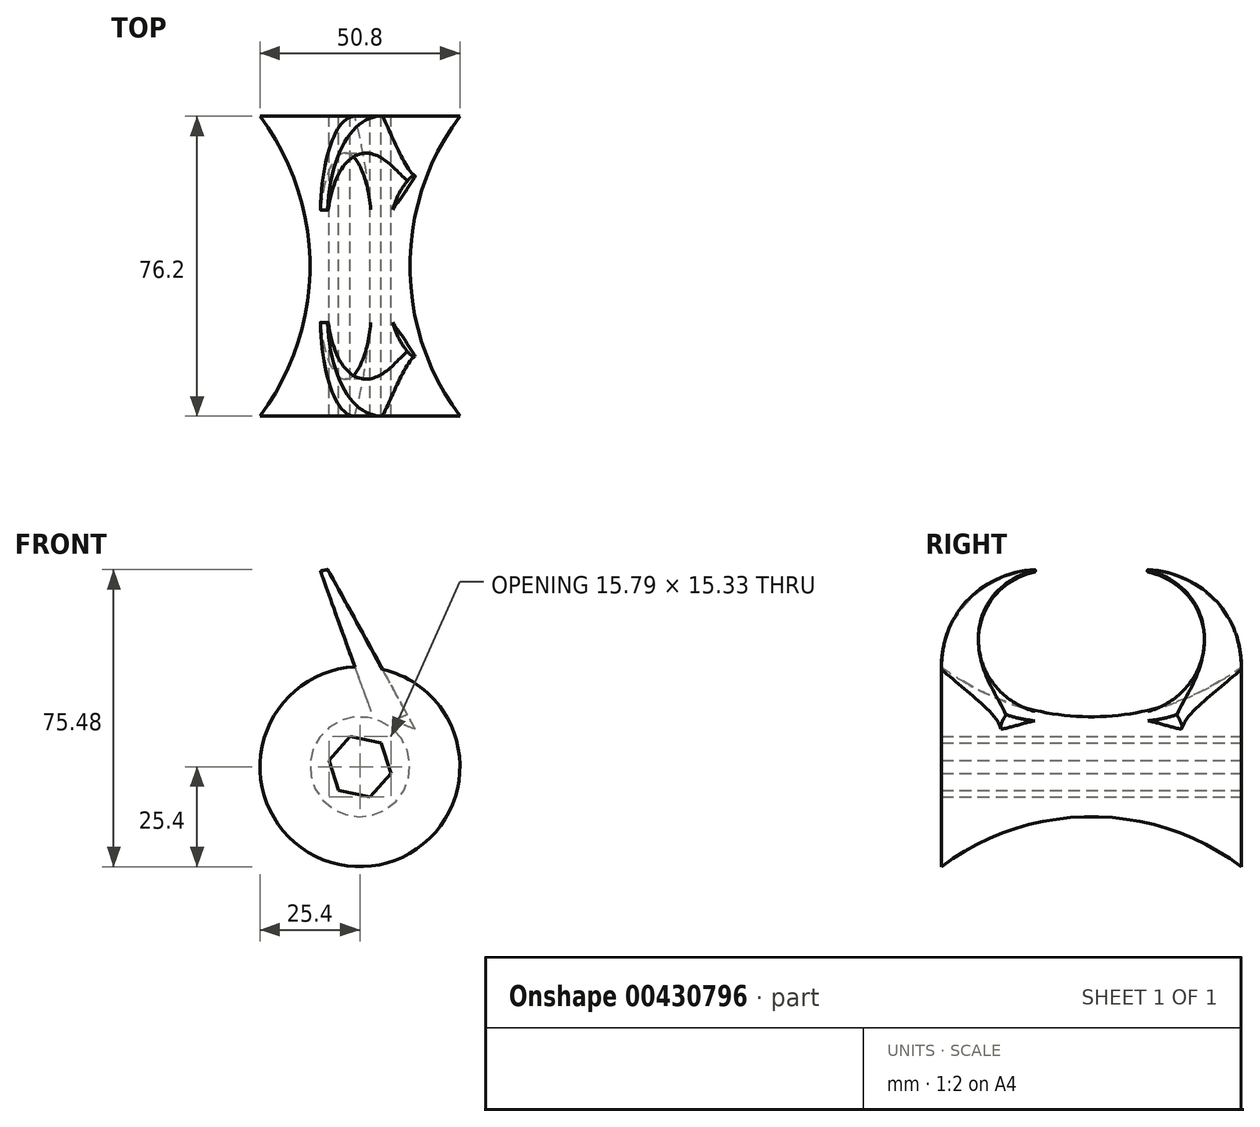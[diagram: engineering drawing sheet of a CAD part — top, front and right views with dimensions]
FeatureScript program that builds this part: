
annotation { "Feature Type Name" : "Feature", "Feature Type Description" : "" }
export const myFeature = defineFeature(function(context is Context, id is Id, definition is map)
    precondition{}
    {
        {
            var Q0;
            Q0=qCreatedBy(makeId("Top.planeOp"),FACE);
            var sketch = newSketch(context, id + "F0", { "sketchPlane" : qUnion([Q0])});
            skLineSegment(sketch, "E0", {"start": v(0, 0) * mm, "end": v(0, 76.2) * mm});
            skLineSegment(sketch, "E1", {"start": v(0, 0) * mm, "end": v(-25.4, 0) * mm});
            skLineSegment(sketch, "E2", {"start": v(0, 76.2) * mm, "end": v(-25.4, 76.2) * mm});
            skArc(sketch, "E3", {"start": v(-25.4, 0) * mm, "mid": v(-12.7, 38.1) * mm, "end": v(-25.4, 76.2) * mm});
            skLineSegment(sketch, "E4", {"start": v(0, 38.1) * mm, "end": v(-6.35, 38.1) * mm, "construction": true});
            skPoint(sketch, "E4.endSnap0", {"position": v(-12.7, 38.1) * mm});
            skSolve(sketch);
        }
        {
            var Q0;
            Q0=makeQuery(id+"F0.imprint","IMPRINT",FACE,{"disambiguationData":[TD([[makeQuery(id+"F0.imprint","IMPRINT",EDGE,{"derivedFrom":sQuery(id+"F0.wireOp",EDGE,"E0")}),1.0]])]});
            var Q1;
            Q1=sQuery(id+"F0.wireOp",EDGE,"E0");
            revolve(context, id + "F1", {"entities" : qUnion([Q0]), "axis" : qUnion([Q1]), "revolveType" : RevolveType.FULL});
        }
        {
            var Q0;
            Q0=makeQuery(id+"F1.opRevolve","SWEPT_FACE",FACE,{"disambiguationData":[OSD([sQuery(id+"F0.wireOp",EDGE,"E2")])]});
            var sketch = newSketch(context, id + "F2", { "sketchPlane" : qUnion([Q0])});
            skCircle(sketch, "E5.cCircle", {"center": v(0, 0) * mm, "radius": 6.99 * mm, "construction": true});
            skLineSegment(sketch, "E5.0", {"start": v(-2.51, -7.66) * mm, "end": v(-7.9, -1.66) * mm});
            skLineSegment(sketch, "E5.1", {"start": v(-7.9, -1.66) * mm, "end": v(-5.38, 6) * mm});
            skLineSegment(sketch, "E5.2", {"start": v(-5.38, 6) * mm, "end": v(2.51, 7.66) * mm});
            skLineSegment(sketch, "E5.3", {"start": v(2.51, 7.66) * mm, "end": v(7.9, 1.66) * mm});
            skLineSegment(sketch, "E5.4", {"start": v(7.9, 1.66) * mm, "end": v(5.38, -6) * mm});
            skLineSegment(sketch, "E5.5", {"start": v(5.38, -6) * mm, "end": v(-2.51, -7.66) * mm});
            skPoint(sketch, "E5.0.midPoint", {"position": v(-5.2, -4.66) * mm});
            skSolve(sketch);
        }
        {
            var Q0;
            Q0 = qSketchRegion(id + "F2", true);
            extrude(context, id + "F3", {"entities" : qUnion([Q0]), "operationType" : NewBodyOperationType.REMOVE, "endBound" : BoundingType.THROUGH_ALL, "oppositeDirection" : true, "depth" : 25.4 * mm});
        }
        {
            var Q0;
            Q0=qCreatedBy(makeId("Right.planeOp"),FACE);
            var sketch = newSketch(context, id + "F4", { "sketchPlane" : qUnion([Q0])});
            skLineSegment(sketch, "E6.top", {"start": v(0, 12.7) * mm, "end": v(76.2, 12.7) * mm});
            skLineSegment(sketch, "E7", {"start": v(38.1, 12.7) * mm, "end": v(38.1, 32.91) * mm});
            skLineSegment(sketch, "E8", {"start": v(23.52, 66.48) * mm, "end": v(0, 66.48) * mm});
            skArc(sketch, "E9", {"start": v(23.75, 14.34) * mm, "mid": v(38.1, 12.7) * mm, "end": v(52.45, 14.34) * mm});
            skLineSegment(sketch, "E10", {"start": v(0, 66.48) * mm, "end": v(0, 25.4) * mm});
            skArc(sketch, "E11", {"start": v(0, 25.4) * mm, "mid": v(38.1, 12.7) * mm, "end": v(76.2, 25.4) * mm});
            skPoint(sketch, "E12", {"position": v(76.2, 25.4) * mm});
            skLineSegment(sketch, "E13", {"start": v(48.9, 66.48) * mm, "end": v(76.2, 66.48) * mm});
            skLineSegment(sketch, "E14", {"start": v(76.2, 66.48) * mm, "end": v(76.2, 25.4) * mm});
            skLineSegment(sketch, "E15.bottom", {"start": v(23.52, 66.48) * mm, "end": v(48.9, 66.48) * mm});
            skArc(sketch, "E16", {"start": v(25.4, 50.8) * mm, "mid": v(9.4, 33.26) * mm, "end": v(23.75, 14.34) * mm});
            skArc(sketch, "E17", {"start": v(25.4, 50.8) * mm, "mid": v(7.44, 43.36) * mm, "end": v(0, 25.4) * mm});
            skArc(sketch, "E18.MirrorCS", {"start": v(50.8, 50.8) * mm, "mid": v(66.8, 33.26) * mm, "end": v(52.45, 14.34) * mm});
            skArc(sketch, "E19.MirrorCS", {"start": v(50.8, 50.8) * mm, "mid": v(68.76, 43.36) * mm, "end": v(76.2, 25.4) * mm});
            skSolve(sketch);
        }
        {
            var Q0;
            Q0=qCreatedBy(makeId("Front.planeOp"),FACE);
            var sketch = newSketch(context, id + "F5", { "sketchPlane" : qUnion([Q0])});
            skLineSegment(sketch, "E20", {"start": v(4.23, 9.95) * mm, "end": v(-13.99, 60.71) * mm});
            skLineSegment(sketch, "E21", {"start": v(-13.99, 60.71) * mm, "end": v(12.04, 13.2) * mm});
            skLineSegment(sketch, "E22", {"start": v(12.04, 13.2) * mm, "end": v(4.23, 9.95) * mm});
            skSolve(sketch);
        }
        {
            var Q0;
            Q0 = qSketchRegion(id + "F5", true);
            var Q1;
            Q1=makeQuery(id+"F1.opRevolve","SWEPT_FACE",FACE,{"disambiguationData":[OSD([sQuery(id+"F0.wireOp",EDGE,"E2")])]});
            extrude(context, id + "F6", {"entities" : qUnion([Q0]), "operationType" : NewBodyOperationType.ADD, "endBound" : BoundingType.UP_TO_SURFACE, "oppositeDirection" : true, "endBoundEntityFace" : qUnion([Q1]), "depth" : 25.4 * mm});
        }
        {
            var Q0;
            Q0=makeQuery(id+"F4.imprint","IMPRINT",FACE,{"disambiguationData":[TD([[makeQuery(id+"F4.imprint","IMPRINT",EDGE,{"derivedFrom":sQuery(id+"F4.wireOp",EDGE,"E8")}),1.0]])]});
            var Q1;
            Q1=sQuery(id+"F0.wireOp",EDGE,"E0");
            revolve(context, id + "F7", {"operationType" : NewBodyOperationType.REMOVE, "entities" : qUnion([Q0]), "axis" : qUnion([Q1]), "revolveType" : RevolveType.FULL, "oppositeDirection" : true});
        }
        {
            var Q0;
            {var subQ0=makeQuery(id+"F1.opRevolve","SWEPT_FACE",FACE,{"disambiguationData":[OSD([sQuery(id+"F0.wireOp",EDGE,"E3")])]});var subQ1=makeQuery(id+"F6.opExtrude","SWEPT_FACE",FACE,{"disambiguationData":[OSD([sQuery(id+"F5.wireOp",EDGE,"E22")])]});Q0=makeQuery(id+"F7.boolean.opBoolean","SPLIT",EDGE,{"disambiguationData":[TD([makeQuery(id+"F7.opRevolve","SWEPT_FACE",FACE,{"disambiguationData":[OSD([sQuery(id+"F4.wireOp",EDGE,"E16")])]})])],"derivedFrom":makeQuery(id+"F6.boolean.opBoolean","INTERSECT",EDGE,{"derivedFrom":[subQ0,subQ1]})});}
            var Q1;
            {var subQ0=makeQuery(id+"F1.opRevolve","SWEPT_FACE",FACE,{"disambiguationData":[OSD([sQuery(id+"F0.wireOp",EDGE,"E3")])]});var subQ1=makeQuery(id+"F6.opExtrude","SWEPT_FACE",FACE,{"disambiguationData":[OSD([sQuery(id+"F5.wireOp",EDGE,"E22")])]});Q1=makeQuery(id+"F7.boolean.opBoolean","SPLIT",EDGE,{"disambiguationData":[TD([makeQuery(id+"F7.opRevolve","SWEPT_FACE",FACE,{"disambiguationData":[OSD([sQuery(id+"F4.wireOp",EDGE,"E18.MirrorCS")])]})])],"derivedFrom":makeQuery(id+"F6.boolean.opBoolean","INTERSECT",EDGE,{"derivedFrom":[subQ0,subQ1]})});}
            fillet(context, id + "F8", {"entities" : qUnion([Q0, Q1]), "radius" : 5.08 * mm, "tangentPropagation" : true, "allowEdgeOverflow" : false});
        }
        {
            var Q0;
            Q0=makeQuery(id+"F7.boolean.opBoolean","COPY",EDGE,{"derivedFrom":makeQuery(id+"F7.opRevolve","SWEPT_EDGE",EDGE,{"disambiguationData":[OSD([sQuery(id+"F4.wireOp",EDGE,"E18.MirrorCS"),sQuery(id+"F4.wireOp",EDGE,"E19.MirrorCS")])]})});
            var Q1;
            Q1=makeQuery(id+"F7.boolean.opBoolean","COPY",EDGE,{"derivedFrom":makeQuery(id+"F7.opRevolve","SWEPT_EDGE",EDGE,{"disambiguationData":[OSD([sQuery(id+"F4.wireOp",EDGE,"E16"),sQuery(id+"F4.wireOp",EDGE,"E17")])]})});
            fillet(context, id + "F9", {"entities" : qUnion([Q0, Q1]), "radius" : 0.13 * mm, "tangentPropagation" : true, "allowEdgeOverflow" : false});
        }
    });
